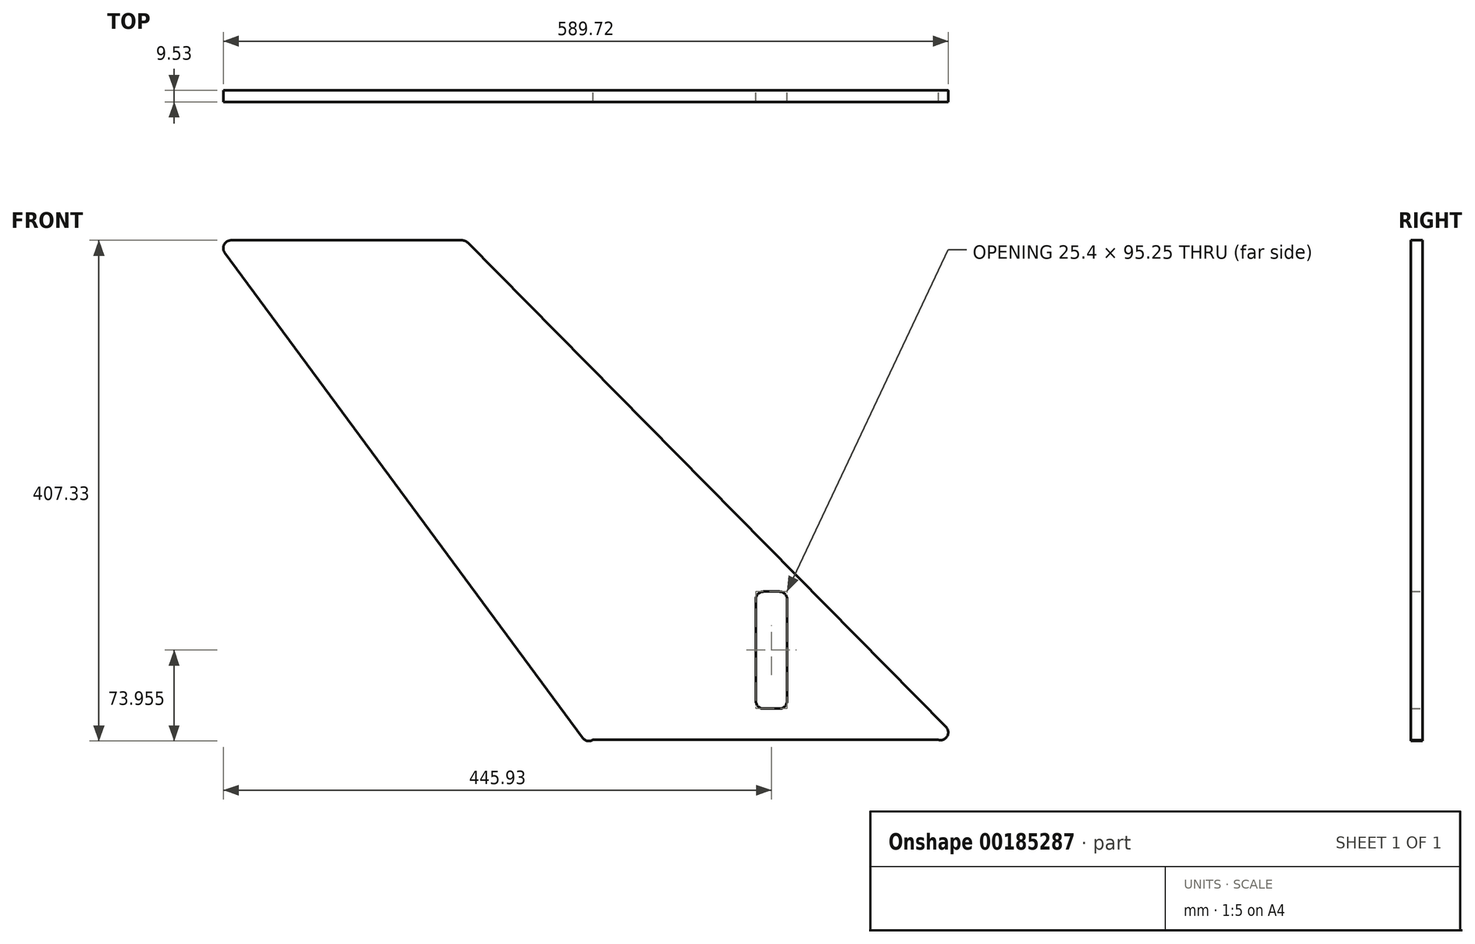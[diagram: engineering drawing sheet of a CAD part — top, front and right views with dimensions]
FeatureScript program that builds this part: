
annotation { "Feature Type Name" : "Feature", "Feature Type Description" : "" }
export const myFeature = defineFeature(function(context is Context, id is Id, definition is map)
    precondition{}
    {
        {
            var Q0;
            Q0=qCreatedBy(makeId("Front.planeOp"),FACE);
            var sketch = newSketch(context, id + "F0", { "sketchPlane" : qUnion([Q0])});
            skLineSegment(sketch, "E0", {"start": v(-1.22, 1.65) * mm, "end": v(-292.3, 396.28) * mm});
            skLineSegment(sketch, "E1", {"start": v(-287.18, 406.4) * mm, "end": v(-99.21, 406.4) * mm});
            skLineSegment(sketch, "E2", {"start": v(-94.7, 404.51) * mm, "end": v(294.35, 10.58) * mm});
            skPoint(sketch, "E3", {"position": v(152.4, 0) * mm});
            skLineSegment(sketch, "E4", {"start": v(152.4, 0) * mm, "end": v(152.4, 120.65) * mm, "construction": true});
            skPoint(sketch, "E5.visualSharp", {"position": v(-299.76, 406.4) * mm});
            skArc(sketch, "E5.filletArc", {"start": v(-287.18, 406.4) * mm, "mid": v(-292.85, 402.91) * mm, "end": v(-292.3, 396.28) * mm});
            skPoint(sketch, "E6.visualSharp", {"position": v(-96.56, 406.4) * mm});
            skArc(sketch, "E6.filletArc", {"start": v(-94.7, 404.51) * mm, "mid": v(-96.76, 405.9) * mm, "end": v(-99.21, 406.4) * mm});
            skPoint(sketch, "E7.visualSharp", {"position": v(0, 0) * mm});
            skArc(sketch, "E7.filletArc", {"start": v(-1.22, 1.65) * mm, "mid": v(2.67, -0.8) * mm, "end": v(7.2, 0) * mm});
            skPoint(sketch, "E8.visualSharp", {"position": v(304.8, 0) * mm});
            skArc(sketch, "E8.filletArc", {"start": v(288.13, 0) * mm, "mid": v(295.3, 2.9) * mm, "end": v(294.35, 10.58) * mm});
            skLineSegment(sketch, "E9", {"start": v(7.2, 0) * mm, "end": v(288.13, 0) * mm});
            skLineSegment(sketch, "E10.bottom", {"start": v(146.05, 25.4) * mm, "end": v(158.75, 25.4) * mm});
            skLineSegment(sketch, "E10.top", {"start": v(146.05, 120.65) * mm, "end": v(158.75, 120.65) * mm});
            skLineSegment(sketch, "E10.left", {"start": v(139.7, 31.75) * mm, "end": v(139.7, 114.3) * mm});
            skLineSegment(sketch, "E10.right", {"start": v(165.1, 31.75) * mm, "end": v(165.1, 114.3) * mm});
            skPoint(sketch, "E11", {"position": v(152.4, 120.65) * mm});
            skPoint(sketch, "E12", {"position": v(152.4, 25.4) * mm});
            skPoint(sketch, "E13.visualSharp", {"position": v(139.7, 120.65) * mm});
            skArc(sketch, "E13.filletArc", {"start": v(146.05, 120.65) * mm, "mid": v(141.56, 118.8) * mm, "end": v(139.7, 114.3) * mm});
            skPoint(sketch, "E14.visualSharp", {"position": v(139.7, 25.4) * mm});
            skArc(sketch, "E14.filletArc", {"start": v(139.7, 31.75) * mm, "mid": v(141.56, 27.26) * mm, "end": v(146.05, 25.4) * mm});
            skPoint(sketch, "E15.visualSharp", {"position": v(165.1, 120.65) * mm});
            skArc(sketch, "E15.filletArc", {"start": v(165.1, 114.3) * mm, "mid": v(163.24, 118.8) * mm, "end": v(158.75, 120.65) * mm});
            skPoint(sketch, "E16.visualSharp", {"position": v(165.1, 25.4) * mm});
            skArc(sketch, "E16.filletArc", {"start": v(158.75, 25.4) * mm, "mid": v(163.24, 27.26) * mm, "end": v(165.1, 31.75) * mm});
            skSolve(sketch);
        }
        {
            var Q0;
            Q0=makeQuery(id+"F0.imprint","IMPRINT",FACE,{"disambiguationData":[TD([[makeQuery(id+"F0.imprint","IMPRINT",EDGE,{"derivedFrom":sQuery(id+"F0.wireOp",EDGE,"E0")}),-1.0]])]});
            extrude(context, id + "F1", {"entities" : qUnion([Q0]), "depth" : 9.52 * mm});
        }
    });
